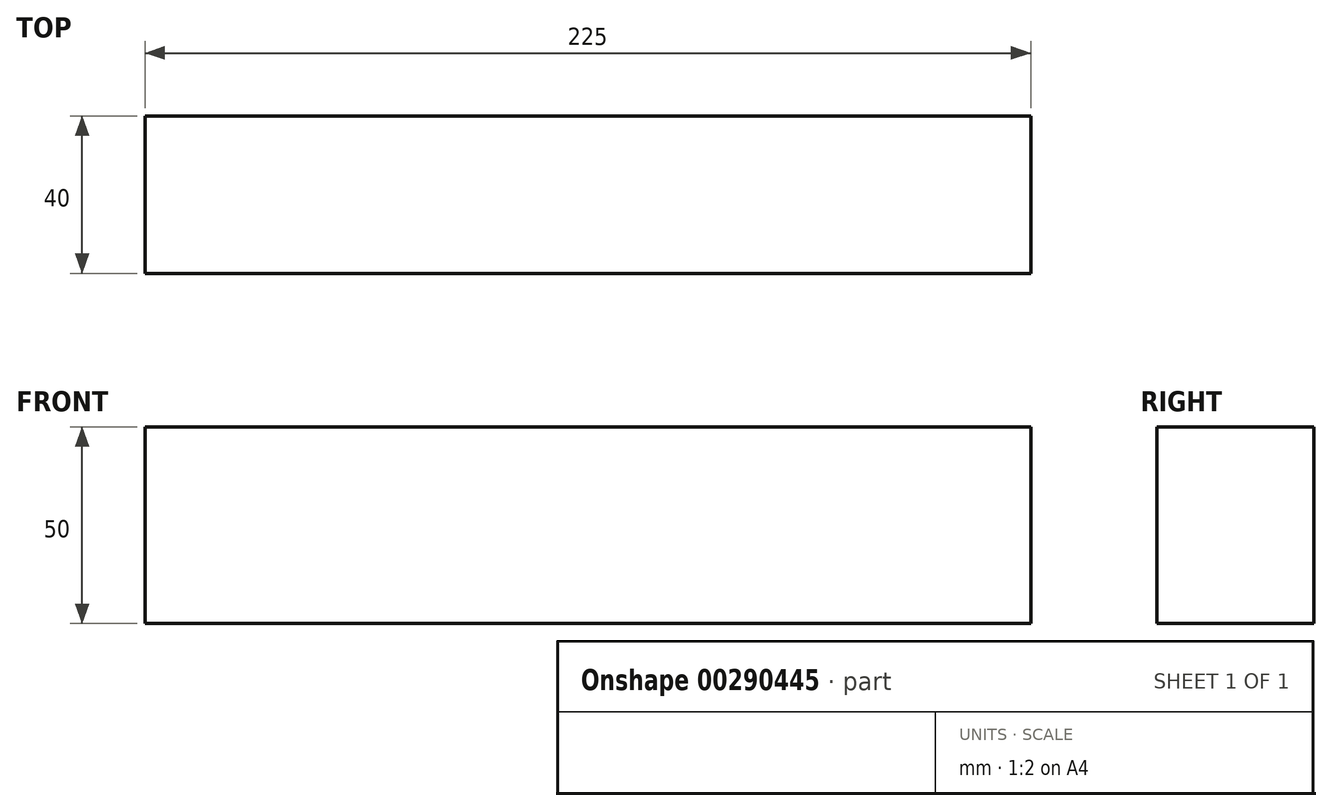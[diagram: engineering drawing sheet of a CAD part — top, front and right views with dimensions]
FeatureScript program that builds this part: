
annotation { "Feature Type Name" : "Feature", "Feature Type Description" : "" }
export const myFeature = defineFeature(function(context is Context, id is Id, definition is map)
    precondition{}
    {
        {
            var Q0;
            Q0=qCreatedBy(makeId("Front.planeOp"),FACE);
            var sketch = newSketch(context, id + "F0", { "sketchPlane" : qUnion([Q0])});
            skLineSegment(sketch, "E0", {"start": v(0, 25) * mm, "end": v(112.5, 25) * mm});
            skLineSegment(sketch, "E1", {"start": v(112.5, 25) * mm, "end": v(112.5, 0) * mm});
            skLineSegment(sketch, "E2.MirrorCS", {"start": v(0, -25) * mm, "end": v(112.5, -25) * mm});
            skLineSegment(sketch, "E3.MirrorCS", {"start": v(112.5, -25) * mm, "end": v(112.5, 0) * mm});
            skLineSegment(sketch, "E4.MirrorCS", {"start": v(-112.5, -25) * mm, "end": v(-112.5, 0) * mm});
            skLineSegment(sketch, "E5.MirrorCS", {"start": v(-112.5, 25) * mm, "end": v(-112.5, 0) * mm});
            skLineSegment(sketch, "E6.MirrorCS", {"start": v(0, -25) * mm, "end": v(-112.5, -25) * mm});
            skLineSegment(sketch, "E7.MirrorCS", {"start": v(0, 25) * mm, "end": v(-112.5, 25) * mm});
            skSolve(sketch);
        }
        {
            var Q0;
            Q0 = qSketchRegion(id + "F0", true);
            extrude(context, id + "F1", {"entities" : qUnion([Q0]), "depth" : 40 * mm});
        }
    });
